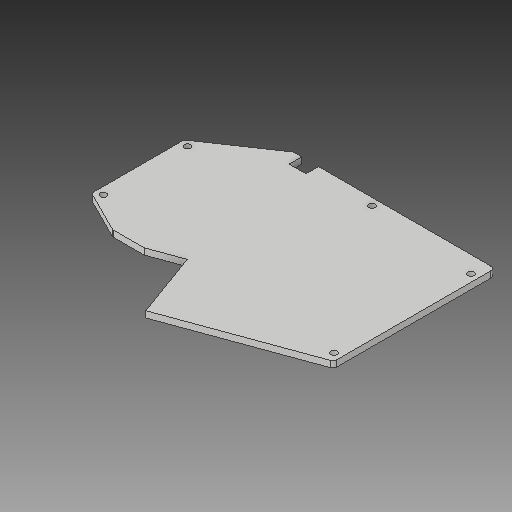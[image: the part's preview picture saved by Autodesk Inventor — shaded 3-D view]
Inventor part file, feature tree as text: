
AUTODESK INVENTOR PART (.ipt)
format: ipt  version: 2017 (Build 210142000, 142)  size: 146,944 bytes
history: native  units: in
note: dims shown in document units (in); Inventor stores cm internally (conversion verified against a paired STEP export)
features: other x3, extrude x1, sketch x1
ambient origin geometry x8: Origin, YZ Plane, XZ Plane, XY Plane, X Axis, Y Axis, Z Axis, Center Point
bodies: Solid5 (feature_tree)
feature tree (5):
  other  "k2_base.ipt"
  extrude  "Extrusion13"  Depth=0.3937in
  other  "Solid5::k2_base.ipt"
  other  "TaggingFeature1"
  sketch  "Sketch12"  dims[d73=0.1575in d178=0.3937in d183=0.3937in d184=0.0in d185=0.6299in]
